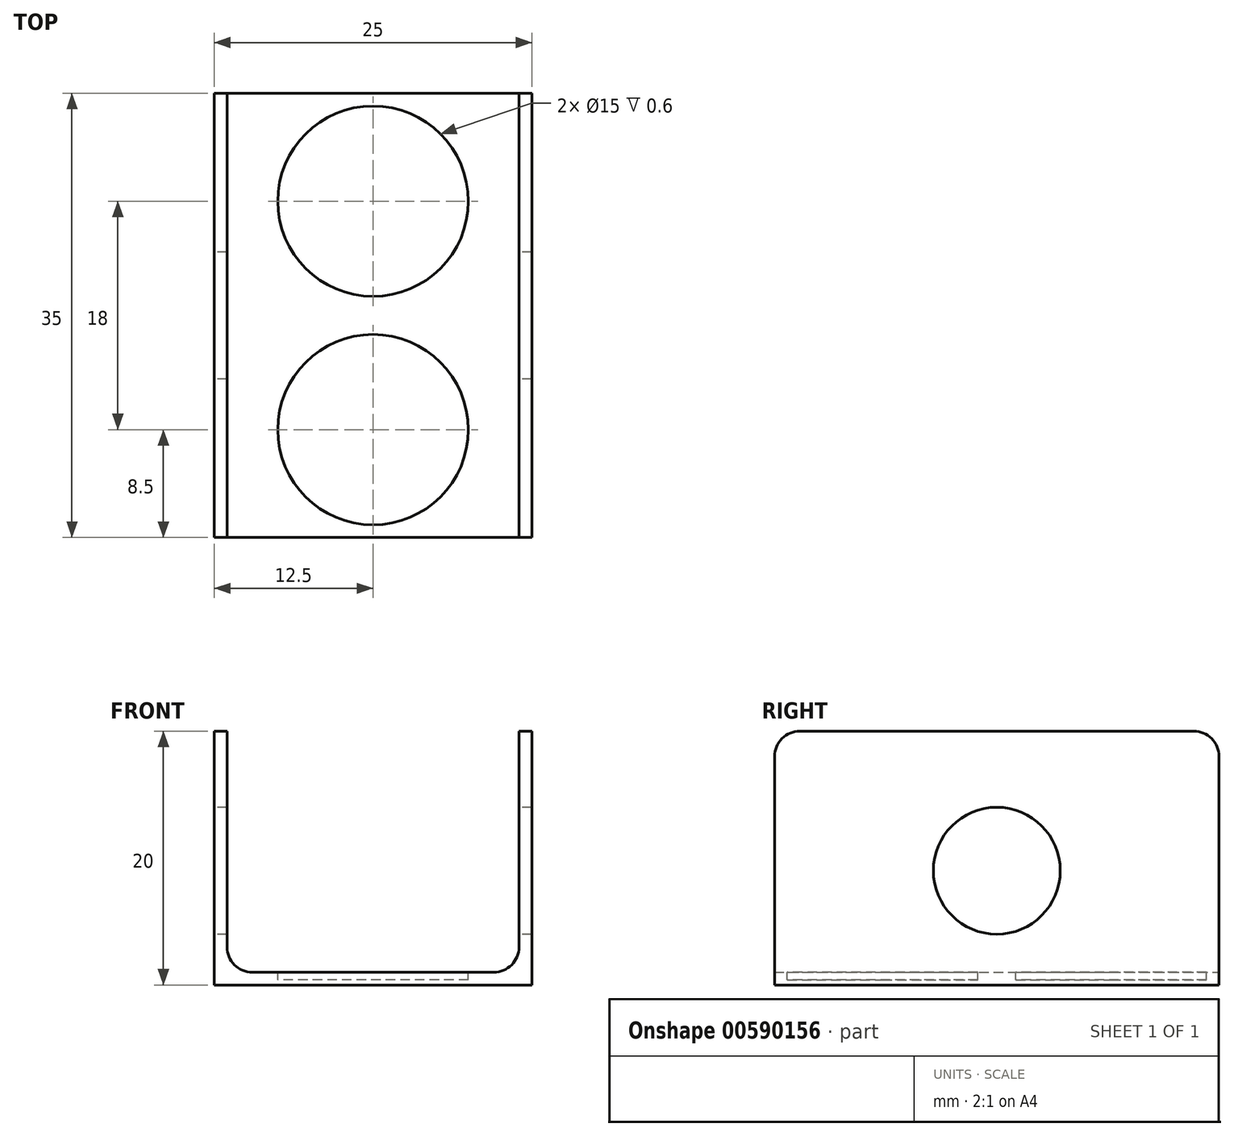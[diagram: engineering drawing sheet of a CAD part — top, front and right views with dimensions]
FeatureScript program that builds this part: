
annotation { "Feature Type Name" : "Feature", "Feature Type Description" : "" }
export const myFeature = defineFeature(function(context is Context, id is Id, definition is map)
    precondition{}
    {
        {
            var Q0;
            Q0=qCreatedBy(makeId("Front.planeOp"),FACE);
            var sketch = newSketch(context, id + "F0", { "sketchPlane" : qUnion([Q0])});
            skLineSegment(sketch, "E0", {"start": v(0, 0) * mm, "end": v(-12.5, 0) * mm});
            skLineSegment(sketch, "E1", {"start": v(-12.5, 0) * mm, "end": v(-12.5, 20) * mm});
            skLineSegment(sketch, "E2", {"start": v(-12.5, 20) * mm, "end": v(-11.5, 20) * mm});
            skLineSegment(sketch, "E3", {"start": v(-11.5, 20) * mm, "end": v(-11.5, 1) * mm});
            skLineSegment(sketch, "E4", {"start": v(-11.5, 1) * mm, "end": v(0, 1) * mm});
            skLineSegment(sketch, "E5.MirrorCS", {"start": v(12.5, 20) * mm, "end": v(11.5, 20) * mm});
            skLineSegment(sketch, "E6.MirrorCS", {"start": v(11.5, 1) * mm, "end": v(0, 1) * mm});
            skLineSegment(sketch, "E7.MirrorCS", {"start": v(11.5, 20) * mm, "end": v(11.5, 1) * mm});
            skLineSegment(sketch, "E8.MirrorCS", {"start": v(0, 0) * mm, "end": v(12.5, 0) * mm});
            skLineSegment(sketch, "E9.MirrorCS", {"start": v(12.5, 0) * mm, "end": v(12.5, 20) * mm});
            skSolve(sketch);
        }
        {
            var Q0;
            Q0 = qSketchRegion(id + "F0", true);
            extrude(context, id + "F1", {"entities" : qUnion([Q0]), "depth" : 35 * mm, "offsetDistance" : 25 * mm});
        }
        {
            var Q0;
            Q0=makeQuery(id+"F1.opExtrude","SWEPT_FACE",FACE,{"disambiguationData":[OSD([sQuery(id+"F0.wireOp",EDGE,"E4"),sQuery(id+"F0.wireOp",EDGE,"E6.MirrorCS")])]});
            var sketch = newSketch(context, id + "F2", { "sketchPlane" : qUnion([Q0])});
            skCircle(sketch, "E10", {"center": v(0, -8.5) * mm, "radius": 7.5 * mm});
            skCircle(sketch, "E11", {"center": v(0, -26.5) * mm, "radius": 7.5 * mm});
            skSolve(sketch);
        }
        {
            var Q0;
            Q0 = qSketchRegion(id + "F2", true);
            extrude(context, id + "F3", {"entities" : qUnion([Q0]), "operationType" : NewBodyOperationType.REMOVE, "oppositeDirection" : true, "depth" : 0.6 * mm, "offsetDistance" : 25 * mm});
        }
        {
            var Q0;
            Q0=makeQuery(id+"F1.opExtrude","SWEPT_EDGE",EDGE,{"disambiguationData":[OSD([sQuery(id+"F0.wireOp",EDGE,"E3"),sQuery(id+"F0.wireOp",EDGE,"E4")])]});
            var Q1;
            Q1=makeQuery(id+"F1.opExtrude","SWEPT_EDGE",EDGE,{"disambiguationData":[OSD([sQuery(id+"F0.wireOp",EDGE,"E6.MirrorCS"),sQuery(id+"F0.wireOp",EDGE,"E7.MirrorCS")])]});
            var Q2;
            Q2=makeQuery(id+"F1.opExtrude","CAP_EDGE",EDGE,{"disambiguationData":[OSD([sQuery(id+"F0.wireOp",EDGE,"E2")])],"isStart":false});
            var Q3;
            Q3=makeQuery(id+"F1.opExtrude","CAP_EDGE",EDGE,{"disambiguationData":[OSD([sQuery(id+"F0.wireOp",EDGE,"E5.MirrorCS")])],"isStart":false});
            var Q4;
            Q4=makeQuery(id+"F1.opExtrude","CAP_EDGE",EDGE,{"disambiguationData":[OSD([sQuery(id+"F0.wireOp",EDGE,"E5.MirrorCS")])],"isStart":true});
            var Q5;
            Q5=makeQuery(id+"F1.opExtrude","CAP_EDGE",EDGE,{"disambiguationData":[OSD([sQuery(id+"F0.wireOp",EDGE,"E2")])],"isStart":true});
            fillet(context, id + "F4", {"entities" : qUnion([Q0, Q1, Q2, Q3, Q4, Q5]), "radius" : 2 * mm, "tangentPropagation" : true, "allowEdgeOverflow" : false});
        }
        {
            var Q0;
            Q0=makeQuery(id+"F1.opExtrude","SWEPT_FACE",FACE,{"disambiguationData":[OSD([sQuery(id+"F0.wireOp",EDGE,"E1")])]});
            var sketch = newSketch(context, id + "F5", { "sketchPlane" : qUnion([Q0])});
            skCircle(sketch, "E12", {"center": v(17.5, 9) * mm, "radius": 5 * mm});
            skPoint(sketch, "E12.centerSnap0", {"position": v(17.5, 20) * mm});
            skPoint(sketch, "E12.centerSnap1", {"position": v(0, 9) * mm});
            skSolve(sketch);
        }
        {
            var Q0;
            Q0 = qSketchRegion(id + "F5", true);
            extrude(context, id + "F6", {"entities" : qUnion([Q0]), "operationType" : NewBodyOperationType.REMOVE, "endBound" : BoundingType.THROUGH_ALL, "oppositeDirection" : true, "depth" : 25 * mm, "offsetDistance" : 25 * mm});
        }
    });
